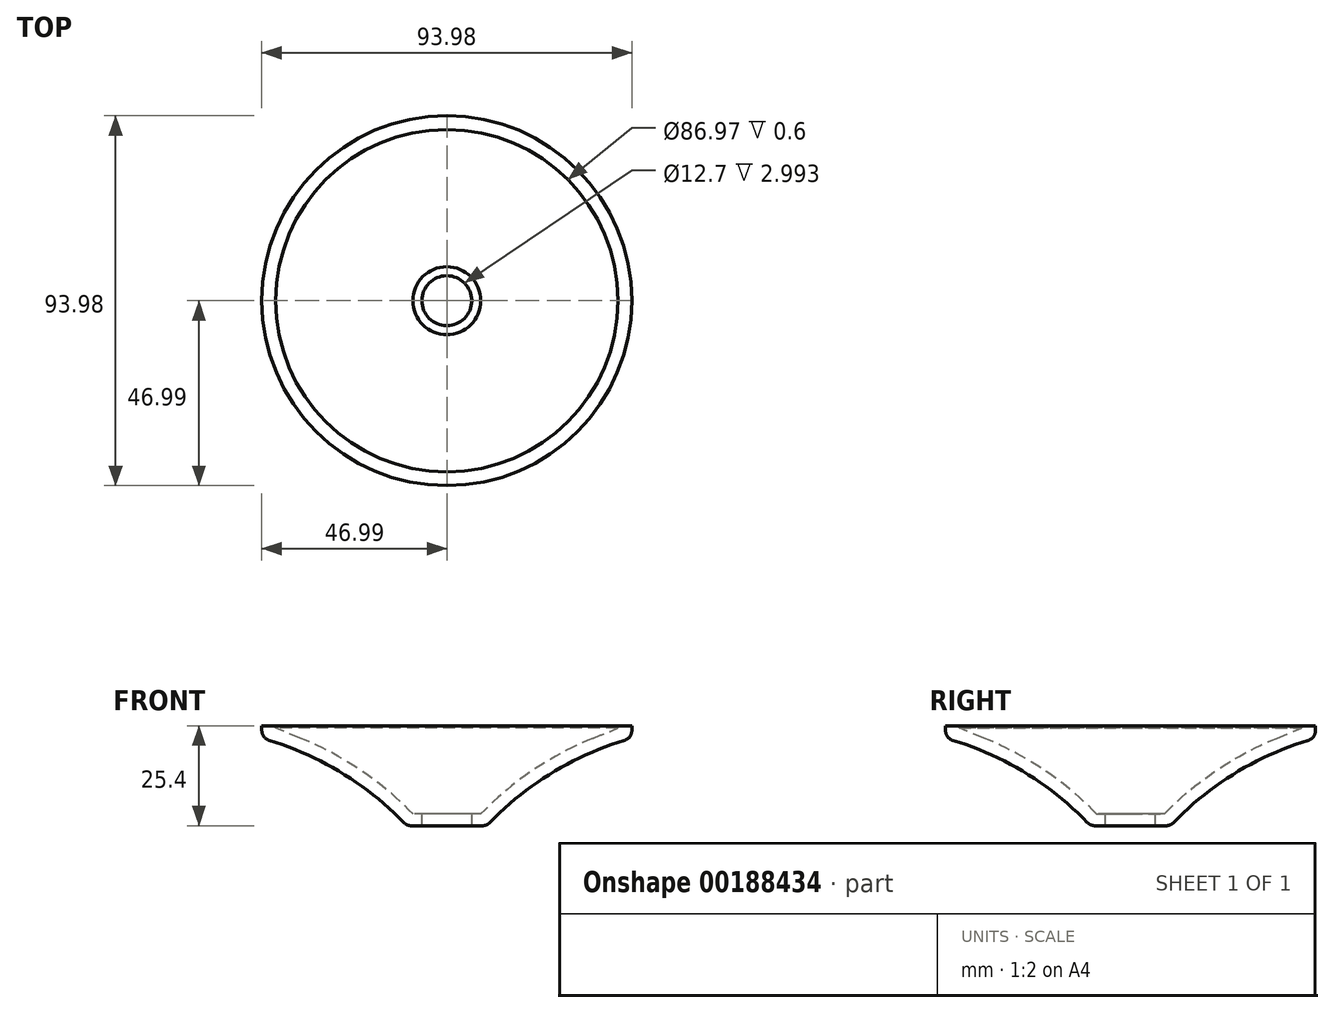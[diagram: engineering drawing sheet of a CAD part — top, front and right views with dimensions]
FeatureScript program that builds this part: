
annotation { "Feature Type Name" : "Feature", "Feature Type Description" : "" }
export const myFeature = defineFeature(function(context is Context, id is Id, definition is map)
    precondition{}
    {
        {
            var Q0;
            Q0=qCreatedBy(makeId("Front.planeOp"),FACE);
            var sketch = newSketch(context, id + "F0", { "sketchPlane" : qUnion([Q0])});
            skLineSegment(sketch, "E0", {"start": v(43.49, -0.13) * mm, "end": v(47, -0.13) * mm});
            skLineSegment(sketch, "E1", {"start": v(47, -0.13) * mm, "end": v(47, -1.4) * mm});
            skLineSegment(sketch, "E2", {"start": v(0, -22.53) * mm, "end": v(0, -25.53) * mm});
            skLineSegment(sketch, "E3", {"start": v(0, -25.53) * mm, "end": v(9.07, -25.53) * mm});
            skArc(sketch, "E4", {"start": v(45.18, -3.82) * mm, "mid": v(26.7, -12.1) * mm, "end": v(10.9, -24.75) * mm});
            skPoint(sketch, "E5.visualSharp", {"position": v(47, -3.3) * mm});
            skArc(sketch, "E5.filletArc", {"start": v(45.18, -3.82) * mm, "mid": v(46.49, -2.9) * mm, "end": v(47, -1.4) * mm});
            skPoint(sketch, "E6.visualSharp", {"position": v(10.16, -25.53) * mm});
            skArc(sketch, "E6.filletArc", {"start": v(9.07, -25.53) * mm, "mid": v(10.06, -25.32) * mm, "end": v(10.9, -24.75) * mm});
            skArc(sketch, "E7.0", {"start": v(37.12, -3.3) * mm, "mid": v(21.87, -11.42) * mm, "end": v(8.63, -22.53) * mm});
            skLineSegment(sketch, "E8", {"start": v(5.72, -25.7) * mm, "end": v(5.72, -25.53) * mm});
            skLineSegment(sketch, "E9", {"start": v(5.72, -22.53) * mm, "end": v(8.63, -22.53) * mm});
            skArc(sketch, "E10.trimOffspring", {"start": v(5.87, -25.53) * mm, "mid": v(5.8, -25.62) * mm, "end": v(5.72, -25.7) * mm});
            skLineSegment(sketch, "E11.trimOffspring", {"start": v(5.72, -25.53) * mm, "end": v(5.72, -25.7) * mm});
            skLineSegment(sketch, "E12", {"start": v(5.72, -22.53) * mm, "end": v(0, -22.53) * mm});
            skLineSegment(sketch, "E13", {"start": v(37.12, -3.3) * mm, "end": v(43.49, -0.73) * mm});
            skLineSegment(sketch, "E14", {"start": v(43.49, -0.73) * mm, "end": v(43.49, -0.13) * mm});
            skSolve(sketch);
        }
        {
            var Q0;
            Q0 = qSketchRegion(id + "F0", true);
            var Q1;
            Q1=sQuery(id+"F0.wireOp",EDGE,"E2");
            revolve(context, id + "F1", {"entities" : qUnion([Q0]), "axis" : qUnion([Q1]), "revolveType" : RevolveType.FULL});
        }
        {
            var Q0;
            Q0=makeQuery(id+"F1.opRevolve","SWEPT_FACE",FACE,{"disambiguationData":[OSD([sQuery(id+"F0.wireOp",EDGE,"E9"),sQuery(id+"F0.wireOp",EDGE,"E12")])]});
            var sketch = newSketch(context, id + "F2", { "sketchPlane" : qUnion([Q0])});
            skCircle(sketch, "E15", {"center": v(0, 0) * mm, "radius": 6.35 * mm});
            skSolve(sketch);
        }
        {
            var Q0;
            Q0 = qSketchRegion(id + "F2", true);
            extrude(context, id + "F3", {"entities" : qUnion([Q0]), "operationType" : NewBodyOperationType.REMOVE, "endBound" : BoundingType.THROUGH_ALL, "oppositeDirection" : true, "depth" : 25.4 * mm});
        }
    });
